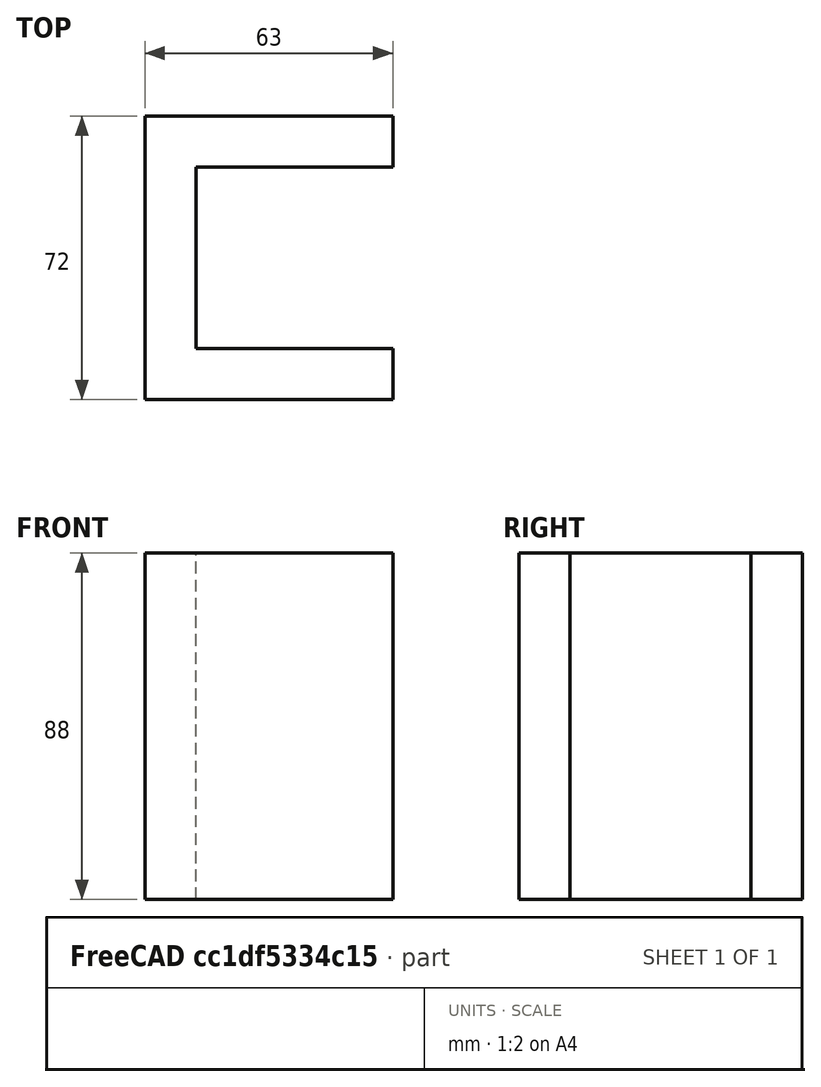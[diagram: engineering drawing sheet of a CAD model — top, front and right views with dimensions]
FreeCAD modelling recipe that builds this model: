
FCSTD DOCUMENT  (FreeCAD 0.17R13522 (Git))
Label: PlateX_01
License: All rights reserved
LicenseURL: http://en.wikipedia.org/wiki/All_rights_reserved
objects: Sketcher::SketchObject×1, Part::Extrusion×1
note: 2 computed .brp shape members not serialized (recipe doc carries the construction recipe); baked Part::Feature solids carry a one-line shape summary decoded from their .brp

FEATURE [Sketcher::SketchObject] Sketch
  sketch-geometry (8):
    g0: LineSegment StartX=62.5368 StartY=100.973 StartZ=0 EndX=62.5368 EndY=28.9731 EndZ=0
    g1: LineSegment StartX=62.5368 StartY=28.9731 StartZ=0 EndX=125.537 EndY=28.9731 EndZ=0
    g2: LineSegment StartX=125.537 StartY=28.9731 StartZ=0 EndX=125.537 EndY=41.9731 EndZ=0
    g3: LineSegment StartX=125.537 StartY=41.9731 StartZ=0 EndX=75.5368 EndY=41.9731 EndZ=0
    g4: LineSegment StartX=75.5368 StartY=41.9731 StartZ=0 EndX=75.5368 EndY=87.9731 EndZ=0
    g5: LineSegment StartX=75.5368 StartY=87.9731 StartZ=0 EndX=125.537 EndY=87.9731 EndZ=0
    g6: LineSegment StartX=125.537 StartY=87.9731 StartZ=0 EndX=125.537 EndY=100.973 EndZ=0
    g7: LineSegment StartX=125.537 StartY=100.973 StartZ=0 EndX=62.5368 EndY=100.973 EndZ=0
  constraints (22):
    c: Vertical(g0)
    c: Coincident(g0,g1)
    c: Horizontal(g1)
    c: Coincident(g1,g2)
    c: Vertical(g2)
    c: Coincident(g2,g3)
    c: Horizontal(g3)
    c: Coincident(g3,g4)
    c: Vertical(g4)
    c: Coincident(g4,g5)
    c: Horizontal(g5)
    c: Coincident(g5,g6)
    c: Coincident(g6,g7)
    c: Coincident(g7,g0)
    c: Horizontal(g7)
    c: Equal(g7,g1)
    c: Equal(g5,g3)
    c: Equal(g6,g2)
    c: DistanceY(g0,g0) = 72
    c: DistanceX(g7,g7) = 63
    c: DistanceX(g5,g5) = 50
    c: DistanceY(g4,g4) = 46
FEATURE [Part::Extrusion] Extrude  label="PlateX_01"
  Base = -> Sketch
  Dir = (0,0,1)
  DirMode = 2
  FaceMakerClass = Part::FaceMakerBullseye
  LengthFwd = 88
  LengthRev = 0
  Solid = true
  Symmetric = false
